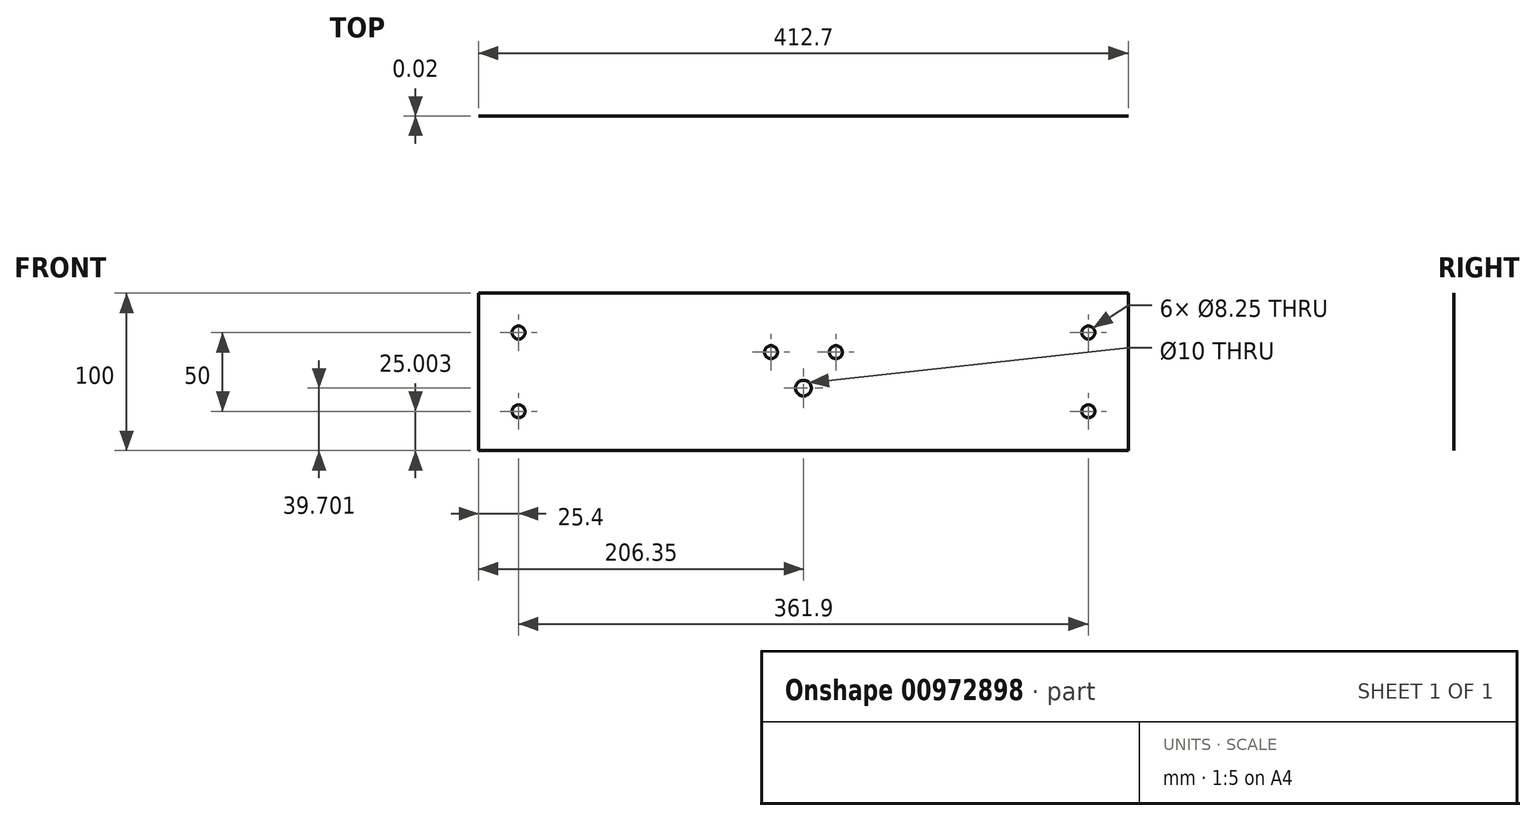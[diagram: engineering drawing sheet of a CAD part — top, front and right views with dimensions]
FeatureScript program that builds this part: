
annotation { "Feature Type Name" : "Feature", "Feature Type Description" : "" }
export const myFeature = defineFeature(function(context is Context, id is Id, definition is map)
    precondition{}
    {
        {
            var Q0;
            Q0=qCreatedBy(makeId("Front.planeOp"),FACE);
            var sketch = newSketch(context, id + "F0", { "sketchPlane" : qUnion([Q0])});
            skCircle(sketch, "E0", {"center": v(-180.95, 32.47) * mm, "radius": 4.12 * mm});
            skCircle(sketch, "E1", {"center": v(-180.95, -17.53) * mm, "radius": 4.12 * mm});
            skCircle(sketch, "E2", {"center": v(0, -2.83) * mm, "radius": 5 * mm});
            skCircle(sketch, "E3", {"center": v(-20.6, 20) * mm, "radius": 4.12 * mm});
            skLineSegment(sketch, "E4", {"start": v(206.35, -42.53) * mm, "end": v(206.35, 57.47) * mm});
            skLineSegment(sketch, "E5", {"start": v(206.35, -42.53) * mm, "end": v(-206.35, -42.53) * mm});
            skLineSegment(sketch, "E6", {"start": v(-206.35, -42.53) * mm, "end": v(-206.35, 57.47) * mm});
            skLineSegment(sketch, "E7", {"start": v(0, 57.47) * mm, "end": v(0, -42.53) * mm, "construction": true});
            skCircle(sketch, "E8.MirrorC", {"center": v(20.6, 20) * mm, "radius": 4.12 * mm});
            skCircle(sketch, "E9.MirrorC", {"center": v(180.95, 32.47) * mm, "radius": 4.12 * mm});
            skCircle(sketch, "E10.MirrorC", {"center": v(180.95, -17.53) * mm, "radius": 4.12 * mm});
            skLineSegment(sketch, "E11", {"start": v(-206.35, 7.47) * mm, "end": v(206.35, 7.47) * mm, "construction": true});
            skLineSegment(sketch, "E12.bottom", {"start": v(-206.35, 57.47) * mm, "end": v(206.35, 57.47) * mm});
            skLineSegment(sketch, "E12.top", {"start": v(-206.35, -42.53) * mm, "end": v(206.35, -42.53) * mm});
            skLineSegment(sketch, "E12.left", {"start": v(-206.35, 57.47) * mm, "end": v(-206.35, -42.53) * mm});
            skLineSegment(sketch, "E12.right", {"start": v(206.35, 57.47) * mm, "end": v(206.35, -42.53) * mm});
            skPoint(sketch, "E12.middle", {"position": v(0, 7.47) * mm});
            skSolve(sketch);
        }
        {
            var Q0;
            Q0=qSketchRegion(id+"F0",true);
            extrude(context, id + "F1", {"entities" : qUnion([Q0]), "depth" : 1 / 50.8 * mm, "offsetDistance" : 25 * mm});
        }
    });
